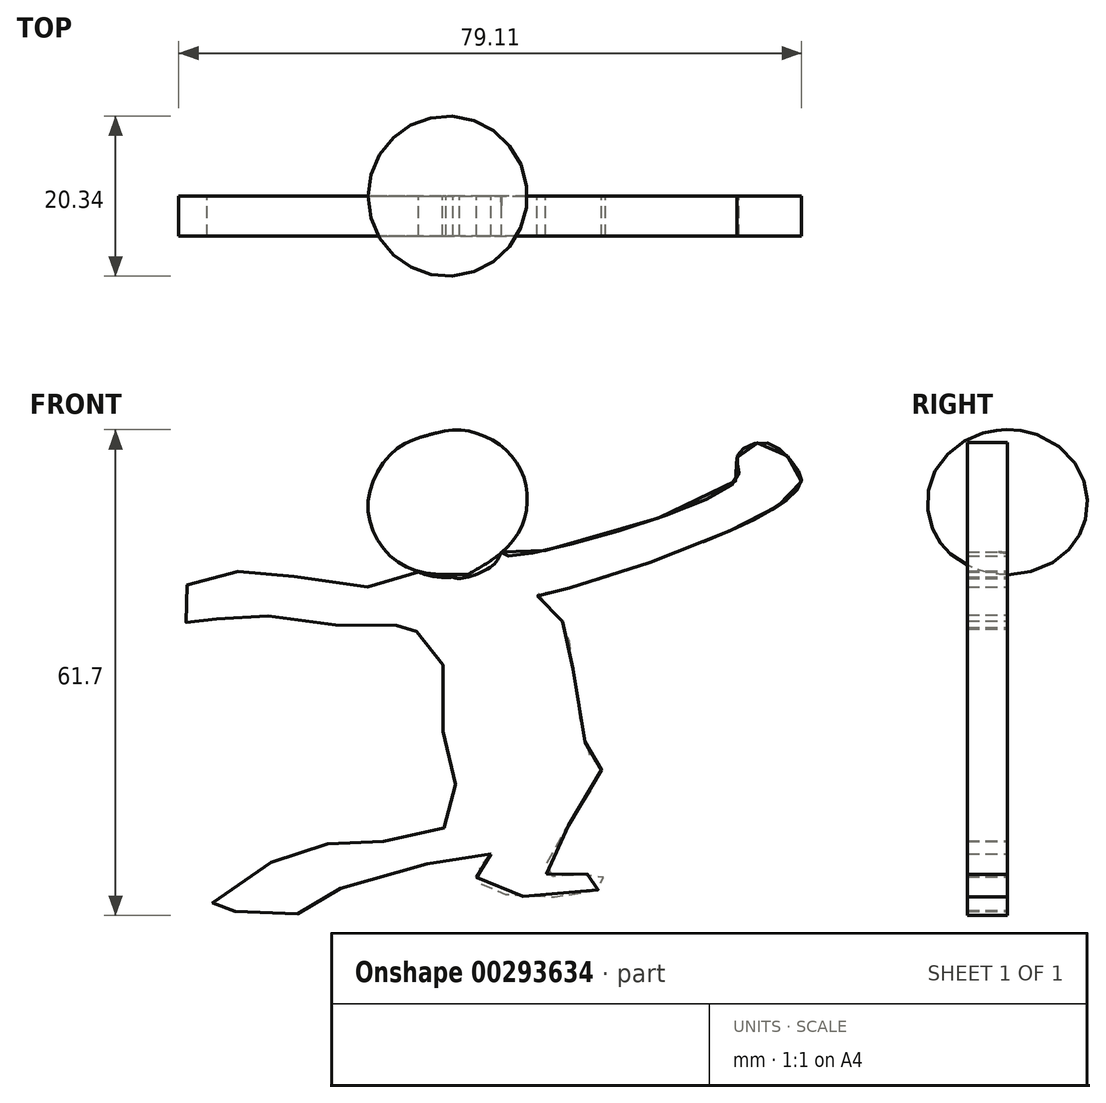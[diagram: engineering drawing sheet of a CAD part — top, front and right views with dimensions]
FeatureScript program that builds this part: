
annotation { "Feature Type Name" : "Feature", "Feature Type Description" : "" }
export const myFeature = defineFeature(function(context is Context, id is Id, definition is map)
    precondition{}
    {
        {
            var Q0;
            Q0=qCreatedBy(makeId("Front.planeOp"),FACE);
            var sketch = newSketch(context, id + "F0", { "sketchPlane" : qUnion([Q0])});
            skArc(sketch, "E0", {"start": v(-9.2, 7) * mm, "mid": v(-7.06, 6.42) * mm, "end": v(-4.85, 6.37) * mm});
            skFitSpline(sketch, "E1", {"points": [v(-9.2, 7) * mm, v(-14.9, 5.16) * mm, v(-26.35, 6.68) * mm, v(-32.65, 7.07) * mm, v(-38.57, 5.35) * mm, v(-39.53, 1.9) * mm, v(-37.62, 0) * mm, v(-35.5, 0.77) * mm, v(-31.06, 1.55) * mm, v(-21.83, 0.62) * mm, v(-12.9, 0) * mm, v(-9.96, 0.77) * mm, v(-9.82, 0) * mm, v(-7.6, -2.24) * mm, v(-5.74, -7.03) * mm, v(-5.88, -17.54) * mm, v(-4.02, -21.2) * mm, v(-6.88, -26.2) * mm, v(-15.55, -27.15) * mm, v(-21.87, -27.75) * mm, v(-30.1, -31.04) * mm, v(-36.04, -35.91) * mm, v(-34.24, -36) * mm, v(-24.95, -36.54) * mm, v(-23.24, -35.37) * mm, v(-9.9, -30.32) * mm, v(0, -28.8) * mm, v(3.52, -22.66) * mm], "startDerivative": vector(-131.53, -67.03) * mm, "endDerivative": vector(63.19, 182.82) * mm});
            skFitSpline(sketch, "E2", {"points": [v(0, -28.8) * mm, v(-1.61, -30.77) * mm, v(-0.9, -33.12) * mm, v(14.16, -33.03) * mm, v(13.98, -31.58) * mm, v(7.76, -31.67) * mm, v(7.13, -29.87) * mm, v(14.07, -18.07) * mm, v(13.08, -17.17) * mm, v(10.28, -4) * mm, v(8.39, 1.67) * mm, v(5.87, 4.1) * mm, v(8.3, 4.64) * mm, v(28.94, 11.67) * mm, v(37.32, 16.04) * mm, v(39.42, 18.5) * mm, v(38.64, 20.43) * mm, v(35.7, 23.26) * mm, v(32.69, 23.02) * mm, v(31.3, 21.76) * mm, v(31.36, 20.5) * mm, v(30.58, 18.09) * mm, v(2.31, 9.07) * mm, v(1.34, 9.56) * mm], "startDerivative": vector(-61.51, -58.64) * mm, "endDerivative": vector(-18.07, 35.38) * mm});
            skFitSpline(sketch, "E3", {"points": [v(1.34, 9.56) * mm, v(0, 7.67) * mm, v(-3.85, 6.22) * mm, v(-4.85, 6.37) * mm], "startDerivative": vector(-2.58, -5.93) * mm, "endDerivative": vector(-3.54, 1.26) * mm});
            skSolve(sketch);
        }
        {
            var Q0;
            Q0 = qSketchRegion(id + "F0", true);
            extrude(context, id + "F1", {"entities" : qUnion([Q0]), "depth" : 5.08 * mm});
        }
        {
            var Q0;
            Q0=qCreatedBy(makeId("Front.planeOp"),FACE);
            var sketch = newSketch(context, id + "F2", { "sketchPlane" : qUnion([Q0])});
            skFitSpline(sketch, "E4", {"points": [v(-7.91, 24.4) * mm, v(-11.42, 23.05) * mm, v(-14.8, 19) * mm, v(-15.47, 13.87) * mm, v(-13.04, 9.28) * mm, v(-8.72, 6.98) * mm, v(-2.92, 6.71) * mm], "startDerivative": vector(-24.63, -6.25) * mm, "endDerivative": vector(33.4, 1.07) * mm});
            skLineSegment(sketch, "E5", {"start": v(-7.91, 24.4) * mm, "end": v(-2.92, 6.71) * mm});
            skSolve(sketch);
        }
        {
            var Q0;
            Q0=makeQuery(id+"F2.imprint","IMPRINT",FACE,{"disambiguationData":[TD([[makeQuery(id+"F2.imprint","IMPRINT",EDGE,{"derivedFrom":sQuery(id+"F2.wireOp",EDGE,"E4")}),1.0]])]});
            var Q1;
            Q1=sQuery(id+"F2.wireOp",EDGE,"E5");
            revolve(context, id + "F3", {"operationType" : NewBodyOperationType.ADD, "entities" : qUnion([Q0]), "axis" : qUnion([Q1]), "revolveType" : RevolveType.FULL});
        }
    });
